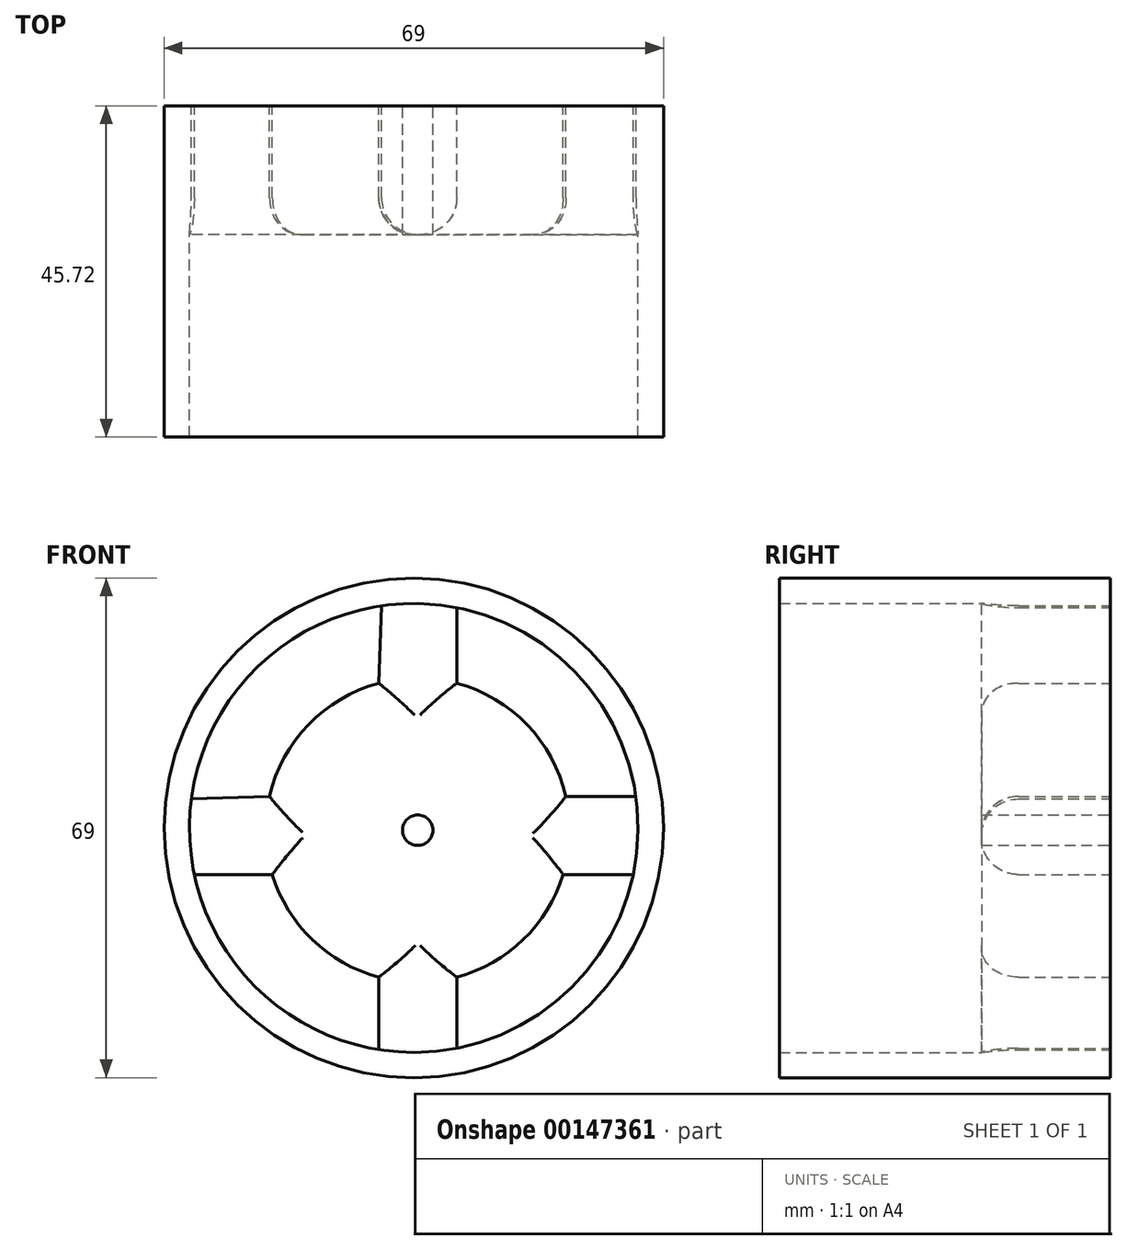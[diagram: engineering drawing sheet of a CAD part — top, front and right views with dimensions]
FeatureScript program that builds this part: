
annotation { "Feature Type Name" : "Feature", "Feature Type Description" : "" }
export const myFeature = defineFeature(function(context is Context, id is Id, definition is map)
    precondition{}
    {
        {
            var Q0;
            Q0=qCreatedBy(makeId("Front.planeOp"),FACE);
            var sketch = newSketch(context, id + "F0", { "sketchPlane" : qUnion([Q0])});
            skCircle(sketch, "E0", {"center": v(-28.7, 22.13) * mm, "radius": 34.5 * mm});
            skCircle(sketch, "E1", {"center": v(-28.7, 22.13) * mm, "radius": 21 * mm});
            skCircle(sketch, "E2", {"center": v(-28.7, 22.13) * mm, "radius": 2 * mm});
            skCircle(sketch, "E3", {"center": v(-28.7, 22.13) * mm, "radius": 31 * mm});
            skLineSegment(sketch, "E4.left", {"start": v(-34.09, 1.83) * mm, "end": v(-34.09, -8.4) * mm});
            skLineSegment(sketch, "E4.right", {"start": v(-28.7, 1.83) * mm, "end": v(-28.7, 1.13) * mm});
            skLineSegment(sketch, "E5.trimOffspring", {"start": v(-28.7, 1.13) * mm, "end": v(-28.7, 1.83) * mm});
            skLineSegment(sketch, "E6.trimOffspring", {"start": v(-23.32, -8.4) * mm, "end": v(-23.32, 1.83) * mm});
            skPoint(sketch, "E7.bottom.start.orphan", {"position": v(-28.7, -12.37) * mm});
            skPoint(sketch, "E8.orphan", {"position": v(-28.7, -8.87) * mm});
            skLineSegment(sketch, "E9.top", {"start": v(-8.61, 16) * mm, "end": v(1.69, 16) * mm});
            skLineSegment(sketch, "E10.top", {"start": v(36.3, 26.78) * mm, "end": v(5.48, 26.78) * mm});
            skLineSegment(sketch, "E11.trimOffspring", {"start": v(2.3, 22.13) * mm, "end": v(5.8, 22.13) * mm});
            skLineSegment(sketch, "E12.trimOffspring", {"start": v(1.95, 26.78) * mm, "end": v(-8.22, 26.78) * mm});
            skPoint(sketch, "E13.orphan", {"position": v(-28.7, 26.78) * mm});
            skLineSegment(sketch, "E14", {"start": v(-28.7, 56.63) * mm, "end": v(-28.7, 56.4) * mm});
            skLineSegment(sketch, "E15.bottom", {"start": v(-28.7, 22.13) * mm, "end": v(-26.7, 22.13) * mm});
            skLineSegment(sketch, "E15.right", {"start": v(-23.32, 42.42) * mm, "end": v(-23.32, 52.65) * mm});
            skPoint(sketch, "E16.orphan", {"position": v(-23.32, 56.2) * mm});
            skPoint(sketch, "E17.orphan", {"position": v(-34.09, 56.2) * mm});
            skLineSegment(sketch, "E18.bottom", {"start": v(-28.7, 22.13) * mm, "end": v(-34.09, 22.13) * mm});
            skLineSegment(sketch, "E18.left", {"start": v(-28.7, 22.13) * mm, "end": v(-28.7, 24.13) * mm});
            skLineSegment(sketch, "E19.bottom", {"start": v(-28.7, 22.13) * mm, "end": v(-30.7, 22.13) * mm});
            skLineSegment(sketch, "E19.top", {"start": v(-48.8, 16) * mm, "end": v(-59.1, 16) * mm});
            skLineSegment(sketch, "E19.left", {"start": v(-28.7, 22.13) * mm, "end": v(-28.7, 20.13) * mm});
            skPoint(sketch, "E18.right.end.orphan", {"position": v(-62.89, 26.78) * mm});
            skPoint(sketch, "E20.orphan", {"position": v(-62.66, 16) * mm});
            skLineSegment(sketch, "E21.trimOffspring", {"start": v(-49.18, 26.78) * mm, "end": v(-59.61, 24.5) * mm});
            skLineSegment(sketch, "E22.trimOffspring", {"start": v(-34.09, 42.42) * mm, "end": v(-31.45, 53) * mm});
            skSolve(sketch);
        }
        {
            var Q0;
            {var subQ0=sQuery(id+"F0.wireOp",EDGE,"E22.trimOffspring");var subQ1=sQuery(id+"F0.wireOp",EDGE,"E0");var subQ2=makeQuery(id+"F0.imprint","INTERSECT",VERTEX,{"derivedFrom":[subQ1,subQ0]});Q0=makeQuery(id+"F0.imprint","IMPRINT",FACE,{"disambiguationData":[TD([[makeQuery(id+"F0.imprint","IMPRINT",EDGE,{"disambiguationData":[TD([[subQ2,-1.0]])],"derivedFrom":subQ1}),-1.0]])]});}
            var Q1;
            {var subQ3=sQuery(id+"F0.wireOp",EDGE,"E0");var subQ7=makeQuery(id+"F0.imprint","IMPRINT",VERTEX,{"derivedFrom":subQ3});Q1=makeQuery(id+"F0.imprint","IMPRINT",FACE,{"disambiguationData":[TD([[makeQuery(id+"F0.imprint","IMPRINT",EDGE,{"disambiguationData":[TD([[subQ7,1.0]])],"derivedFrom":subQ3}),-1.0]])]});}
            var Q2;
            {var subQ0=sQuery(id+"F0.wireOp",EDGE,"E12.trimOffspring");var subQ1=sQuery(id+"F0.wireOp",EDGE,"E0");var subQ2=makeQuery(id+"F0.imprint","INTERSECT",VERTEX,{"derivedFrom":[subQ1,subQ0]});Q2=makeQuery(id+"F0.imprint","IMPRINT",FACE,{"disambiguationData":[TD([[makeQuery(id+"F0.imprint","IMPRINT",EDGE,{"disambiguationData":[TD([[subQ2,-1.0]])],"derivedFrom":subQ1}),-1.0]])]});}
            var Q3;
            {var subQ0=sQuery(id+"F0.wireOp",EDGE,"E11.trimOffspring");Q3=makeQuery(id+"F0.imprint","IMPRINT",FACE,{"disambiguationData":[TD([[makeQuery(id+"F0.imprint","IMPRINT",EDGE,{"derivedFrom":subQ0}),-1.0]])]});}
            var Q4;
            {var subQ0=sQuery(id+"F0.wireOp",EDGE,"E11.trimOffspring");Q4=makeQuery(id+"F0.imprint","IMPRINT",FACE,{"disambiguationData":[TD([[makeQuery(id+"F0.imprint","IMPRINT",EDGE,{"derivedFrom":subQ0}),1.0]])]});}
            var Q5;
            {var subQ0=sQuery(id+"F0.wireOp",EDGE,"E6.trimOffspring");var subQ1=sQuery(id+"F0.wireOp",EDGE,"E0");var subQ2=makeQuery(id+"F0.imprint","INTERSECT",VERTEX,{"derivedFrom":[subQ1,subQ0]});Q5=makeQuery(id+"F0.imprint","IMPRINT",FACE,{"disambiguationData":[TD([[makeQuery(id+"F0.imprint","IMPRINT",EDGE,{"disambiguationData":[TD([[subQ2,-1.0]])],"derivedFrom":subQ1}),-1.0]])]});}
            var Q6;
            {var subQ0=sQuery(id+"F0.wireOp",EDGE,"E21.trimOffspring");var subQ1=sQuery(id+"F0.wireOp",EDGE,"E0");var subQ2=makeQuery(id+"F0.imprint","INTERSECT",VERTEX,{"derivedFrom":[subQ1,subQ0]});Q6=makeQuery(id+"F0.imprint","IMPRINT",FACE,{"disambiguationData":[TD([[makeQuery(id+"F0.imprint","IMPRINT",EDGE,{"disambiguationData":[TD([[subQ2,-1.0]])],"derivedFrom":subQ1}),-1.0]])]});}
            var Q7;
            {var subQ3=sQuery(id+"F0.wireOp",EDGE,"E0");var subQ9=makeQuery(id+"F0.imprint","IMPRINT",VERTEX,{"disambiguationData":[OD(2.0)],"derivedFrom":subQ3});Q7=makeQuery(id+"F0.imprint","IMPRINT",FACE,{"disambiguationData":[TD([[makeQuery(id+"F0.imprint","IMPRINT",EDGE,{"disambiguationData":[TD([[subQ9,1.0]])],"derivedFrom":subQ3}),1.0]])]});}
            extrude(context, id + "F1", {"entities" : qUnion([Q0, Q1, Q2, Q3, Q4, Q5, Q6, Q7]), "depth" : 45.72 * mm});
        }
        {
            var Q0;
            Q0=qCreatedBy(makeId("Front.planeOp"),FACE);
            var sketch = newSketch(context, id + "F2", { "sketchPlane" : qUnion([Q0])});
            skCircle(sketch, "E23", {"center": v(-28.16, 21.8) * mm, "radius": 53.34 * mm});
            skCircle(sketch, "E24", {"center": v(-28.16, 21.8) * mm, "radius": 21 * mm});
            skCircle(sketch, "E25", {"center": v(-28.16, 21.8) * mm, "radius": 2.1 * mm});
            skCircle(sketch, "E26", {"center": v(-28.16, 21.8) * mm, "radius": 49.24 * mm});
            skLineSegment(sketch, "E27.left", {"start": v(-33.54, 1.51) * mm, "end": v(-33.54, -27.14) * mm});
            skLineSegment(sketch, "E27.right", {"start": v(-28.16, 1.51) * mm, "end": v(-28.16, 0.8) * mm});
            skLineSegment(sketch, "E28.right", {"start": v(-22.77, -31.26) * mm, "end": v(-22.77, -28) * mm});
            skLineSegment(sketch, "E29.trimOffspring", {"start": v(-28.16, 0.8) * mm, "end": v(-28.16, 16.7) * mm});
            skLineSegment(sketch, "E30.trimOffspring", {"start": v(-33.54, -28) * mm, "end": v(-33.54, -31.26) * mm});
            skLineSegment(sketch, "E31.trimOffspring", {"start": v(-22.77, -27.14) * mm, "end": v(-22.77, 1.51) * mm});
            skPoint(sketch, "E28.bottom.start.orphan", {"position": v(-28.16, -31.53) * mm});
            skPoint(sketch, "E32.orphan", {"position": v(-28.16, -27.43) * mm});
            skLineSegment(sketch, "E33.trimOffspring", {"start": v(-28.16, 16.7) * mm, "end": v(-28.16, 0.8) * mm});
            skLineSegment(sketch, "E34.top", {"start": v(-8.07, 15.69) * mm, "end": v(20.7, 15.69) * mm});
            skLineSegment(sketch, "E35.top", {"start": v(39.82, 26.46) * mm, "end": v(24.98, 26.46) * mm});
            skLineSegment(sketch, "E36.trimOffspring", {"start": v(21.08, 21.8) * mm, "end": v(25.18, 21.8) * mm});
            skLineSegment(sketch, "E37.trimOffspring", {"start": v(20.86, 26.46) * mm, "end": v(-7.68, 26.46) * mm});
            skPoint(sketch, "E38.orphan", {"position": v(-28.16, 26.46) * mm});
            skLineSegment(sketch, "E39", {"start": v(-28.16, 90.12) * mm, "end": v(-28.16, 75.15) * mm});
            skLineSegment(sketch, "E40.bottom", {"start": v(-28.16, 21.8) * mm, "end": v(-26.06, 21.8) * mm});
            skLineSegment(sketch, "E40.right", {"start": v(-22.77, 42.1) * mm, "end": v(-22.77, 70.75) * mm});
            skPoint(sketch, "E41.orphan", {"position": v(-22.77, 74.88) * mm});
            skPoint(sketch, "E42.orphan", {"position": v(-33.54, 74.88) * mm});
            skLineSegment(sketch, "E43.bottom", {"start": v(-28.16, 21.8) * mm, "end": v(-30.57, 21.8) * mm});
            skLineSegment(sketch, "E43.left", {"start": v(-28.16, 21.8) * mm, "end": v(-28.16, 23.9) * mm});
            skLineSegment(sketch, "E44.bottom", {"start": v(-28.16, 21.8) * mm, "end": v(-30.26, 21.8) * mm});
            skLineSegment(sketch, "E44.top", {"start": v(-48.25, 15.69) * mm, "end": v(-77.02, 15.69) * mm});
            skLineSegment(sketch, "E44.left", {"start": v(-28.16, 21.8) * mm, "end": v(-28.16, 19.7) * mm});
            skPoint(sketch, "E43.right.end.orphan", {"position": v(-81.3, 26.46) * mm});
            skPoint(sketch, "E45.orphan", {"position": v(-81.14, 15.69) * mm});
            skLineSegment(sketch, "E46.trimOffspring", {"start": v(-48.64, 26.46) * mm, "end": v(-77.25, 25.58) * mm});
            skLineSegment(sketch, "E47.trimOffspring", {"start": v(-33.54, 42.1) * mm, "end": v(-32.53, 70.86) * mm});
            skLineSegment(sketch, "E48", {"start": v(-60.9, 26.08) * mm, "end": v(-60.57, 15.69) * mm});
            skLineSegment(sketch, "E49", {"start": v(-33.54, -10.16) * mm, "end": v(-22.77, -10.16) * mm});
            skLineSegment(sketch, "E50", {"start": v(4.15, 15.69) * mm, "end": v(4.15, 26.46) * mm});
            skLineSegment(sketch, "E51", {"start": v(-22.77, 54.7) * mm, "end": v(-33.1, 54.7) * mm});
            skSolve(sketch);
        }
        {
            var Q0;
            {var subQ5=sQuery(id+"F2.wireOp",EDGE,"E48");Q0=makeQuery(id+"F2.imprint","IMPRINT",FACE,{"disambiguationData":[TD([[makeQuery(id+"F2.imprint","IMPRINT",EDGE,{"derivedFrom":subQ5}),1.0]])]});}
            var Q1;
            {var subQ5=sQuery(id+"F2.wireOp",EDGE,"E50");Q1=makeQuery(id+"F2.imprint","IMPRINT",FACE,{"disambiguationData":[TD([[makeQuery(id+"F2.imprint","IMPRINT",EDGE,{"derivedFrom":subQ5}),1.0]])]});}
            var Q2;
            {var subQ5=sQuery(id+"F2.wireOp",EDGE,"E51");Q2=makeQuery(id+"F2.imprint","IMPRINT",FACE,{"disambiguationData":[TD([[makeQuery(id+"F2.imprint","IMPRINT",EDGE,{"derivedFrom":subQ5}),1.0]])]});}
            var Q3;
            {var subQ3=sQuery(id+"F2.wireOp",EDGE,"E24");var subQ8=makeQuery(id+"F2.imprint","IMPRINT",VERTEX,{"derivedFrom":subQ3});Q3=makeQuery(id+"F2.imprint","IMPRINT",FACE,{"disambiguationData":[TD([[makeQuery(id+"F2.imprint","IMPRINT",EDGE,{"disambiguationData":[TD([[subQ8,1.0]])],"derivedFrom":subQ3}),1.0]])]});}
            var Q4;
            {var subQ3=sQuery(id+"F2.wireOp",EDGE,"E49");Q4=makeQuery(id+"F2.imprint","IMPRINT",FACE,{"disambiguationData":[TD([[makeQuery(id+"F2.imprint","IMPRINT",EDGE,{"derivedFrom":subQ3}),1.0]])]});}
            extrude(context, id + "F3", {"entities" : qUnion([Q0, Q1, Q2, Q3, Q4]), "operationType" : NewBodyOperationType.ADD, "depth" : 17.78 * mm});
        }
        {
            var Q0;
            {var subQ0=sQuery(id+"F2.wireOp",EDGE,"E24");Q0=makeQuery(id+"F3.opExtrude","CAP_EDGE",EDGE,{"disambiguationData":[OSD([subQ0]),TDD([makeQuery(id+"F2.imprint","IMPRINT",EDGE,{"disambiguationData":[TD([[makeQuery(id+"F2.imprint","INTERSECT",VERTEX,{"derivedFrom":[subQ0,sQuery(id+"F2.wireOp",EDGE,"E27.left")]}),1.0]])],"derivedFrom":subQ0})])],"isStart":false});}
            var Q1;
            {var subQ0=sQuery(id+"F2.wireOp",EDGE,"E24");Q1=makeQuery(id+"F3.opExtrude","CAP_EDGE",EDGE,{"disambiguationData":[OSD([subQ0]),TDD([makeQuery(id+"F2.imprint","IMPRINT",EDGE,{"disambiguationData":[TD([[makeQuery(id+"F2.imprint","INTERSECT",VERTEX,{"derivedFrom":[subQ0,sQuery(id+"F2.wireOp",EDGE,"E31.trimOffspring")]}),-1.0]])],"derivedFrom":subQ0})])],"isStart":false});}
            var Q2;
            {var subQ0=sQuery(id+"F2.wireOp",EDGE,"E24");Q2=makeQuery(id+"F3.opExtrude","CAP_EDGE",EDGE,{"disambiguationData":[OSD([subQ0]),TDD([makeQuery(id+"F2.imprint","IMPRINT",EDGE,{"disambiguationData":[TD([[makeQuery(id+"F2.imprint","INTERSECT",VERTEX,{"derivedFrom":[subQ0,sQuery(id+"F2.wireOp",EDGE,"E37.trimOffspring")]}),-1.0]])],"derivedFrom":subQ0})])],"isStart":false});}
            var Q3;
            {var subQ0=sQuery(id+"F2.wireOp",EDGE,"E24");Q3=makeQuery(id+"F3.opExtrude","CAP_EDGE",EDGE,{"disambiguationData":[OSD([subQ0]),TDD([makeQuery(id+"F2.imprint","IMPRINT",EDGE,{"disambiguationData":[TD([[makeQuery(id+"F2.imprint","INTERSECT",VERTEX,{"derivedFrom":[subQ0,sQuery(id+"F2.wireOp",EDGE,"E46.trimOffspring")]}),1.0]])],"derivedFrom":subQ0})])],"isStart":false});}
            var Q4;
            Q4=makeQuery(id+"F3.opExtrude","CAP_EDGE",EDGE,{"disambiguationData":[OSD([sQuery(id+"F2.wireOp",EDGE,"E44.top")])],"isStart":false});
            var Q5;
            Q5=makeQuery(id+"F3.opExtrude","CAP_EDGE",EDGE,{"disambiguationData":[OSD([sQuery(id+"F2.wireOp",EDGE,"E46.trimOffspring")])],"isStart":false});
            var Q6;
            Q6=makeQuery(id+"F3.opExtrude","CAP_EDGE",EDGE,{"disambiguationData":[OSD([sQuery(id+"F2.wireOp",EDGE,"E40.right")])],"isStart":false});
            var Q7;
            Q7=makeQuery(id+"F3.opExtrude","CAP_EDGE",EDGE,{"disambiguationData":[OSD([sQuery(id+"F2.wireOp",EDGE,"E47.trimOffspring")])],"isStart":false});
            var Q8;
            Q8=makeQuery(id+"F3.opExtrude","CAP_EDGE",EDGE,{"disambiguationData":[OSD([sQuery(id+"F2.wireOp",EDGE,"E27.left"),sQuery(id+"F2.wireOp",EDGE,"E30.trimOffspring")])],"isStart":false});
            var Q9;
            Q9=makeQuery(id+"F3.opExtrude","CAP_EDGE",EDGE,{"disambiguationData":[OSD([sQuery(id+"F2.wireOp",EDGE,"E34.top")])],"isStart":false});
            var Q10;
            Q10=makeQuery(id+"F3.opExtrude","CAP_EDGE",EDGE,{"disambiguationData":[OSD([sQuery(id+"F2.wireOp",EDGE,"E37.trimOffspring")])],"isStart":false});
            var Q11;
            Q11=makeQuery(id+"F3.opExtrude","CAP_EDGE",EDGE,{"disambiguationData":[OSD([sQuery(id+"F2.wireOp",EDGE,"E31.trimOffspring")])],"isStart":false});
            fillet(context, id + "F4", {"entities" : qUnion([Q0, Q1, Q2, Q3, Q4, Q5, Q6, Q7, Q8, Q9, Q10, Q11]), "radius" : 5.08 * mm, "tangentPropagation" : true, "allowEdgeOverflow" : false});
        }
    });
